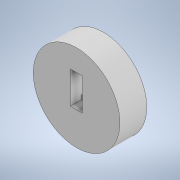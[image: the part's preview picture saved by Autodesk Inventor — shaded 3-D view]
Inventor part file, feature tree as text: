
AUTODESK INVENTOR PART (.ipt)
format: ipt  version: 2021 (Build 250183000, 183)  size: 139,264 bytes
history: native  units: mm
features: extrude x4, sketch x4
ambient origin geometry x8: Origin, YZ Plane, XZ Plane, XY Plane, X Axis, Y Axis, Z Axis, Center Point
bodies: Solid1 (feature_tree)
feature tree (8):
  extrude  "Extrusion1"  Depth=46.5mm TaperAngle=0.0deg
  extrude  "Extrusion2"  Depth=40.5mm
  extrude  "Extrusion3"  Depth=10.25mm
  extrude  "Extrusion4"  Depth=5.0mm
  sketch  "Sketch1"  dims[d0=150.0mm d1=46.5mm d2=0.0mm]
  sketch  "Sketch2"  dims[d5=20.5mm d6=40.5mm]
  sketch  "Sketch4"  dims[d8=10.125mm d9=10.25mm]
  sketch  "Sketch5"  dims[d10=6.5mm d11=5.0mm d12=0.0mm d13=7.0mm d14=46.5mm d15=0.0mm d16=5.0mm d17=0.75mm d18=2.5mm d19=0.0mm d20=55.5mm d21=7.5mm d22=19.0mm d23=0.0mm]
